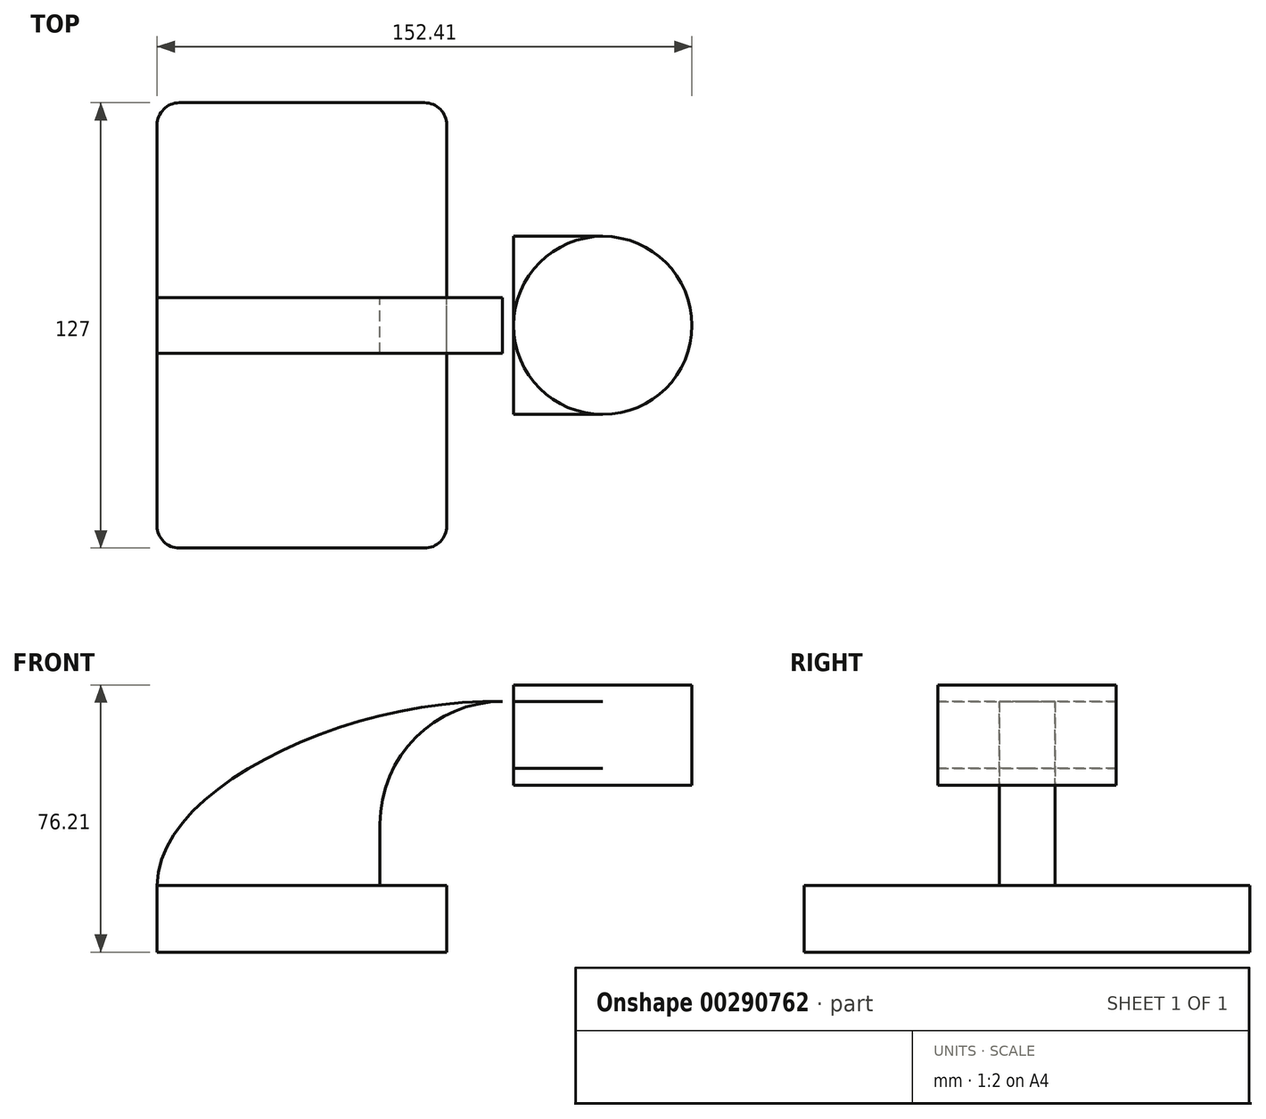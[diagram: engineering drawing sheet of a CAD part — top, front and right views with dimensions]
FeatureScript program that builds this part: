
annotation { "Feature Type Name" : "Feature", "Feature Type Description" : "" }
export const myFeature = defineFeature(function(context is Context, id is Id, definition is map)
    precondition{}
    {
        {
            var Q0;
            Q0=qCreatedBy(makeId("Front.planeOp"),FACE);
            var sketch = newSketch(context, id + "F0", { "sketchPlane" : qUnion([Q0])});
            skLineSegment(sketch, "E0.bottom", {"start": v(41.27, 9.53) * mm, "end": v(-41.28, 9.53) * mm});
            skLineSegment(sketch, "E0.top", {"start": v(41.28, -9.52) * mm, "end": v(-41.27, -9.52) * mm});
            skLineSegment(sketch, "E0.left", {"start": v(41.28, 9.53) * mm, "end": v(41.28, -9.52) * mm});
            skLineSegment(sketch, "E0.right", {"start": v(-41.28, 9.53) * mm, "end": v(-41.27, -9.52) * mm});
            skPoint(sketch, "E0.middle", {"position": v(0, 0) * mm});
            skLineSegment(sketch, "E1.bottom", {"start": v(111.12, 66.68) * mm, "end": v(60.32, 66.68) * mm});
            skLineSegment(sketch, "E1.top", {"start": v(111.12, 38.1) * mm, "end": v(60.32, 38.1) * mm});
            skLineSegment(sketch, "E1.left", {"start": v(111.12, 66.68) * mm, "end": v(111.12, 38.1) * mm});
            skLineSegment(sketch, "E1.right", {"start": v(60.32, 66.68) * mm, "end": v(60.32, 38.1) * mm});
            skPoint(sketch, "E1.middle", {"position": v(85.72, 52.39) * mm});
            skLineSegment(sketch, "E2", {"start": v(41.27, 9.53) * mm, "end": v(41.27, 27) * mm});
            skLineSegment(sketch, "E3", {"start": v(41.27, 27) * mm, "end": v(41.27, 9.53) * mm});
            skArc(sketch, "E4", {"start": v(41.27, 27) * mm, "mid": v(45.92, 38.23) * mm, "end": v(57.15, 42.88) * mm});
            skLineSegment(sketch, "E5", {"start": v(57.15, 42.88) * mm, "end": v(85.72, 42.88) * mm});
            skLineSegment(sketch, "E6.0", {"start": v(22.22, 27) * mm, "end": v(22.23, 9.53) * mm});
            skArc(sketch, "E6.1", {"start": v(22.23, 27) * mm, "mid": v(32.45, 51.7) * mm, "end": v(57.15, 61.93) * mm});
            skLineSegment(sketch, "E6.2", {"start": v(57.15, 61.93) * mm, "end": v(85.72, 61.93) * mm});
            skFitSpline(sketch, "E7", {"points": [v(-41.28, 9.52) * mm, v(57.15, 61.93) * mm], "startDerivative": vector(0.38, 84.89) * mm, "endDerivative": vector(128.99, -3.3) * mm});
            skLineSegment(sketch, "E8", {"start": v(85.72, 66.68) * mm, "end": v(85.72, 38.1) * mm});
            skSolve(sketch);
        }
        {
            var Q0;
            Q0=makeQuery(id+"F0.imprint","IMPRINT",FACE,{"disambiguationData":[TD([[makeQuery(id+"F0.imprint","IMPRINT",EDGE,{"derivedFrom":sQuery(id+"F0.wireOp",EDGE,"E0.top")}),-1.0]])]});
            extrude(context, id + "F1", {"entities" : qUnion([Q0]), "endBound" : BoundingType.SYMMETRIC, "depth" : 127 * mm});
        }
        {
            var Q0;
            {var subQ2=sQuery(id+"F0.wireOp",EDGE,"E6.0");Q0=makeQuery(id+"F0.imprint","IMPRINT",FACE,{"disambiguationData":[TD([[makeQuery(id+"F0.imprint","IMPRINT",EDGE,{"derivedFrom":subQ2}),-1.0]])]});}
            extrude(context, id + "F2", {"entities" : qUnion([Q0]), "operationType" : NewBodyOperationType.ADD, "endBound" : BoundingType.SYMMETRIC, "depth" : 15.88 * mm});
        }
        {
            var Q0;
            {var subQ1=sQuery(id+"F0.wireOp",EDGE,"E3");Q0=makeQuery(id+"F0.imprint","IMPRINT",FACE,{"disambiguationData":[TD([[makeQuery(id+"F0.imprint","IMPRINT",EDGE,{"derivedFrom":subQ1}),-1.0]])]});}
            var Q1;
            {var subQ0=sQuery(id+"F0.wireOp",EDGE,"E6.2");var subQ1=sQuery(id+"F0.wireOp",EDGE,"E1.right");var subQ2=makeQuery(id+"F0.imprint","INTERSECT",VERTEX,{"derivedFrom":[subQ1,subQ0]});Q1=makeQuery(id+"F0.imprint","IMPRINT",FACE,{"disambiguationData":[TD([[makeQuery(id+"F0.imprint","IMPRINT",EDGE,{"disambiguationData":[TD([[subQ2,-1.0]])],"derivedFrom":subQ1}),1.0]])]});}
            extrude(context, id + "F3", {"entities" : qUnion([Q0, Q1]), "operationType" : NewBodyOperationType.ADD, "endBound" : BoundingType.SYMMETRIC, "depth" : 50.8 * mm});
        }
        {
            var Q0;
            {var subQ0=sQuery(id+"F0.wireOp",EDGE,"E1.left");Q0=makeQuery(id+"F0.imprint","IMPRINT",FACE,{"disambiguationData":[TD([[makeQuery(id+"F0.imprint","IMPRINT",EDGE,{"derivedFrom":subQ0}),-1.0]])]});}
            var Q1;
            Q1=sQuery(id+"F0.wireOp",EDGE,"E8");
            revolve(context, id + "F4", {"operationType" : NewBodyOperationType.ADD, "entities" : qUnion([Q0]), "axis" : qUnion([Q1]), "revolveType" : RevolveType.FULL});
        }
        {
            var Q0;
            Q0=makeQuery(id+"F1.opExtrude","CAP_EDGE",EDGE,{"disambiguationData":[OSD([sQuery(id+"F0.wireOp",EDGE,"E0.right")])],"isStart":false});
            var Q1;
            Q1=makeQuery(id+"F1.opExtrude","CAP_EDGE",EDGE,{"disambiguationData":[OSD([sQuery(id+"F0.wireOp",EDGE,"E0.left")])],"isStart":false});
            var Q2;
            Q2=makeQuery(id+"F1.opExtrude","CAP_EDGE",EDGE,{"disambiguationData":[OSD([sQuery(id+"F0.wireOp",EDGE,"E0.right")])],"isStart":true});
            var Q3;
            Q3=makeQuery(id+"F1.opExtrude","CAP_EDGE",EDGE,{"disambiguationData":[OSD([sQuery(id+"F0.wireOp",EDGE,"E0.left")])],"isStart":true});
            fillet(context, id + "F5", {"entities" : qUnion([Q0, Q1, Q2, Q3]), "radius" : 6.35 * mm, "tangentPropagation" : true, "allowEdgeOverflow" : false});
        }
    });
